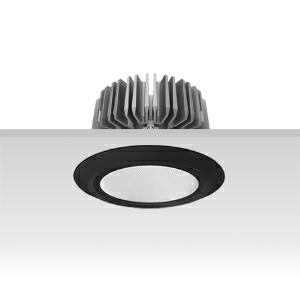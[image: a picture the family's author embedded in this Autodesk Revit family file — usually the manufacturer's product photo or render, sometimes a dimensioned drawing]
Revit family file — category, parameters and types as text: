
# Revit family: 3f_filippi_-_3f_reno_bianco_ampio_3f_filippi_-_30358_a01047_-_3f_reno_150_wh_2000-840_ep_wide___smp_bk_d376
name_source: partatom
category: Lighting Fixtures
units: mm (PartAtom-declared; Revit-internal decimal feet)

## family parameters
Cut with Voids When Loaded = No
Host = Face
Light Source = No
Part Type = Normal
Room Calculation Point = No
Round Connector Dimension = Use Diameter
Shared = No

## types (1)
- 3F Filippi - 3F Reno Bianco Ampio (1 x LED, 1726 lm, 21 W, 4000 K)
    Apparent Load = 21 VA
    Approval mark = ENEC
    CIE Flux Codes = 73 92 98 100 100
    Color Rendering = 80
    Color Temperature = 4000 K
    Control Gear = Electronic ballast
    Default Elevation = 1800 mm
    Description = ILLUMINOTECHNICAL
Luminous efficiency 100% (DLOR 100%, ULOR 0%).
Initial luminous flux of the luminaire 1726 lm.
Emergency luminaire luminous flux BLF 20%.
Direct symmetric wide distribution.
Installation Interdistance Transv.D = 1.01 x hu - Long.D = 1.00 x hu.
Tabular UGR (CIE 117 - 4H-8H; S=0.25H; 70/50/20): RUG 23.4 - 23.4.
Beam angle: 70° - 70°.
Luminous efficacy 82 lm/W.
Lifetime (L90/B10): 30000 h. (tq+25°C)
Lifetime (L85/B10): 50000 h. (tq+25°C)
Lifetime (L70/B10): 80000 h. (tq+25°C)
Sudden decreased luminous flux after 50000 hours: 0% (C0).
Photobiological safety in compliance with IEC/TR 62778: RG0 risk exempt, (IEC 62471).
In compliance with IEC/EN 62722-2-1 - IEC/EN 62717 standards.

SOURCE
Compact LED module 2000/840.
Energy efficiency class (UE 2019/2020 - UE 2019/2015): D.
CIE 13.3 Colour rendering index: CRI >80 (R9 <50%).
IES TM-30 Fidelity Index: Rf = 84 Rg = 95.
CCT nominal colour temperature 4000 K.
Colour initial tolerance (MacAdam): SDCM 3.
Zhaga Book 3 compliant.

MECHANICAL
Passive heat dissipator in die-casting aluminium, oversized, for optimum thermal management of the LED module.
Parabolic element with graduated/concentric rings in white polycarbonate.
Transparent external lens with glossy and satin differentiated surfaces, with a cooling and anti-insect system in methacrylate (PMMA).
Fastening spring clips in stainless steel.
Dimensions: diameter 176 mm, height 111 mm. Weight 1.24 kg.
IP44 protection degree for exposed part, IP20 for recessed part.
Mechanical strength to impacts IK05 (0.7 joule).
Glow-wire test resistance 650°C.

ELECTRICAL
Wiring on a separate unit.
Halogen Free electronic wiring 230V-50/60Hz, power factor 0.90, THD <25%, constant output current, SELV, class II, 1 driver.
Power of the luminaire 21 W.
CE - IEC 60598-1 - EN 60598-1.
EP maintained emergency wiring on board, 1h duration, 24h recharge; compliant with EN 60598-2-22, excluding high risk areas.
SAFE FLICKER: PstLM=<1 and SVM=<0.4 (IEC TR 61547-1 and IEC TR 63158), to ensure a more comfortable and safe light.
Ambient temperature from +5°C to +25°C.
Temperature class T6 max 85°C.
Relative humidity UR: <85%.

INSTALLATION
Pull-up recessed fitting.
False ceiling carving: 150 mm.
All accessories dedicated to this product are available on the Catalog and on our website www.3F-Filippi.com.

ACCESSORIES
A01047 - Anti-glare microprismatic SMP diffuser in methacrylate (PMMA), locked and in line with the trim, in black polycarbonate.

APPLICATIONS
Suitable product for food production plants (HACCP), IFS (Food Version 6), BRC (GSFS Food Version 7).
Environments: architectural, commercial, exhibition areas, transit areas, corridors, shops, display windows, service areas.
In false ceilings with narrow voids.

WARNING
Luminaire designed for disposal/recycling at end-of-life.
Replaceable (LED only) light source by a professional. Replaceable control gear by a professional.
    Height = 0 mm  [stored 0 ft]
    Lamp = 1 x LED
    Lamp Light Flux = 1726 lm
    Lamp Power = 21 W
    Lamp count = 1
    Length = 176 mm
    Lifetime = 50000 h
    Luminous efficacy = 82 lm/W
    Manufacturer = 3F Filippi
    ModVariant = No
    Model = 3F Filippi - 30358+A01047 - 3F Reno 150 WH 2000-840 EP WIDE + SMP BK
    Mounting Place = Ceiling
    Mounting Type = Recessed
    Number of Poles = 1
    OnlyDefault = Yes
    Power Factor = 1
    Product Name = 3F Filippi - 3F Reno Bianco Ampio
    Product group = recessed luminaire
    ProductGroupID = 4
    Protection Class = Protection class II
    Protection Degree = IP 20
    RLX_Detail_Level = 1
    RLX_Emergency_Light_Flux = 0 lm
    RLX_Emergency_Type = 0
    RLX_Emergency_Type_DB = No
    RlxData = <blob elided: 85065 chars, md5=2eac2d3e>
    Socket = socket
    Standby Power = 0 W
    System Light Flux = 1726 lm
    System Power = 21 W
    Type Comments = Product without accessories
    Type Image = 3ffilippi_3f_reno_150_bk_vs_smp.jpg
    URL = http://relux.com
    VarID = ---
    Voltage = 0 V
    Weight = 0.00 kg
    Width = 0 mm  [stored 0 ft]

note: [stored X ft] marks values corroborated as IEEE doubles in the binary element streams (Revit-internal decimal feet)

## geometry (parser evidence)
native form markers: Blend x4, Sweep x9
no freeform markers — native parametric forms only
